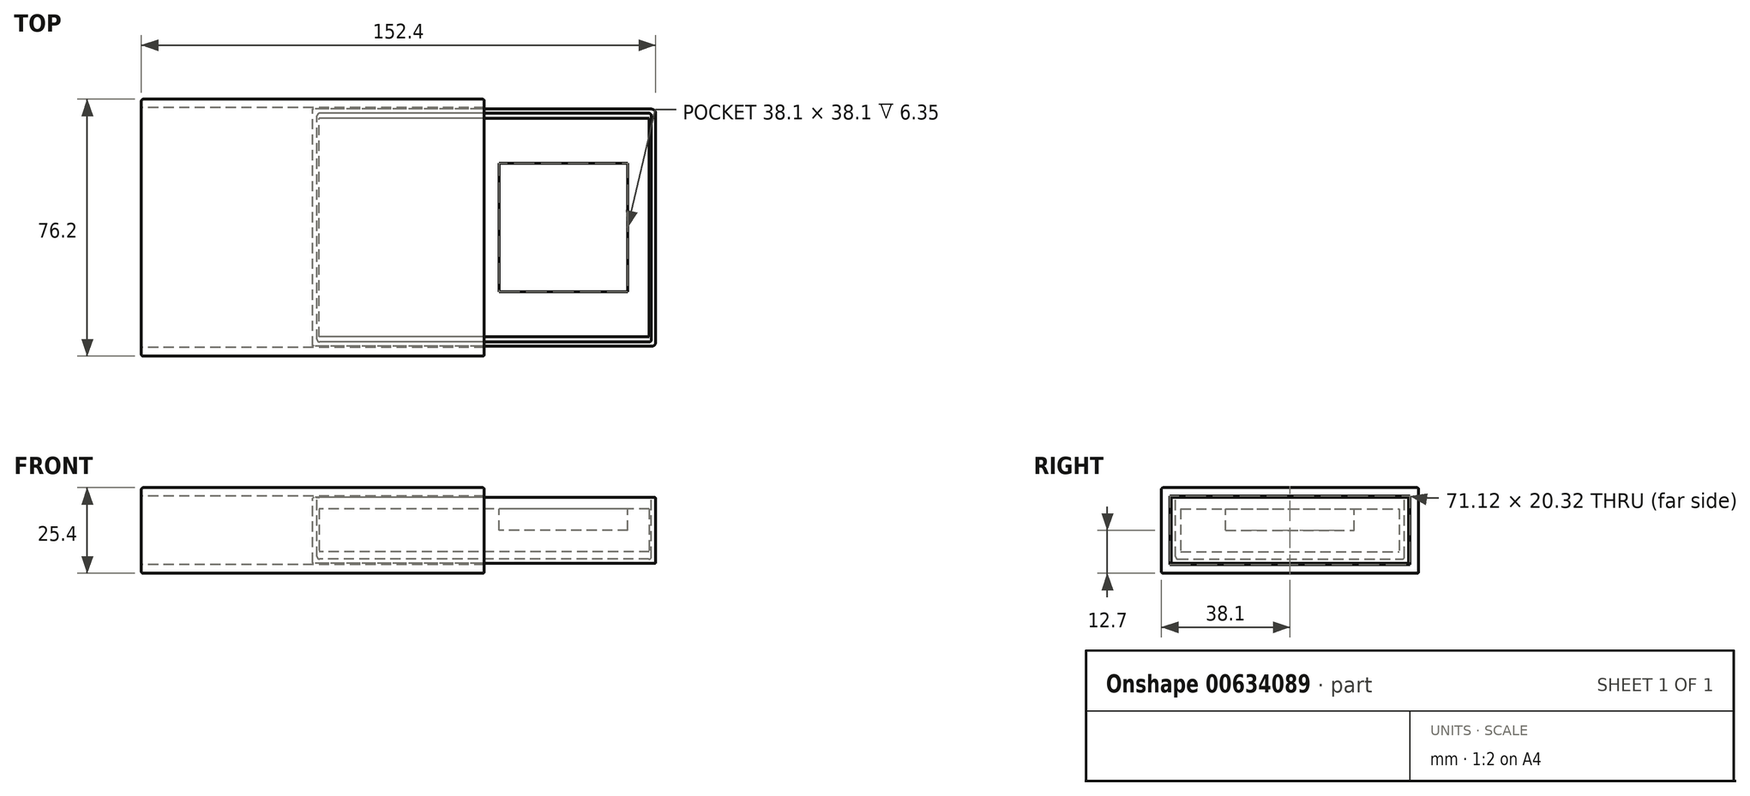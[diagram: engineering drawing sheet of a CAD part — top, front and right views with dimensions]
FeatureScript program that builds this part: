
annotation { "Feature Type Name" : "Feature", "Feature Type Description" : "" }
export const myFeature = defineFeature(function(context is Context, id is Id, definition is map)
    precondition{}
    {
        {
            var Q0;
            Q0=qCreatedBy(makeId("Front.planeOp"),FACE);
            var sketch = newSketch(context, id + "F0", { "sketchPlane" : qUnion([Q0])});
            skLineSegment(sketch, "E0.bottom", {"start": v(50.8, -12.7) * mm, "end": v(-50.8, -12.7) * mm});
            skLineSegment(sketch, "E0.top", {"start": v(50.8, 12.7) * mm, "end": v(-50.8, 12.7) * mm});
            skLineSegment(sketch, "E0.left", {"start": v(50.8, -12.7) * mm, "end": v(50.8, 12.7) * mm});
            skLineSegment(sketch, "E0.right", {"start": v(-50.8, -12.7) * mm, "end": v(-50.8, 12.7) * mm});
            skPoint(sketch, "E0.middle", {"position": v(0, 0) * mm});
            skSolve(sketch);
        }
        {
            var Q0;
            Q0 = qSketchRegion(id + "F0", true);
            extrude(context, id + "F1", {"entities" : qUnion([Q0]), "endBound" : BoundingType.SYMMETRIC, "depth" : 76.2 * mm, "offsetDistance" : 25.4 * mm});
        }
        {
            var Q0;
            Q0=makeQuery(id+"F1.opExtrude","SWEPT_FACE",FACE,{"disambiguationData":[OSD([sQuery(id+"F0.wireOp",EDGE,"E0.left")])]});
            var Q1;
            Q1=makeQuery(id+"F1.opExtrude","SWEPT_FACE",FACE,{"disambiguationData":[OSD([sQuery(id+"F0.wireOp",EDGE,"E0.right")])]});
            shell(context, id + "F2", {"entities" : qUnion([Q0, Q1]), "thickness" : 2.54 * mm});
        }
        {
            var Q0;
            Q0=makeQuery(id+"F1.opExtrude","SWEPT_FACE",FACE,{"disambiguationData":[OSD([sQuery(id+"F0.wireOp",EDGE,"E0.top")])]});
            var Q1;
            Q1=makeQuery(id+"F1.opExtrude","SWEPT_FACE",FACE,{"disambiguationData":[OSD([sQuery(id+"F0.wireOp",EDGE,"E0.bottom")])]});
            var Q2;
            Q2=makeQuery(id+"F1.opExtrude","CAP_EDGE",EDGE,{"disambiguationData":[OSD([sQuery(id+"F0.wireOp",EDGE,"E0.left")])],"isStart":false});
            var Q3;
            Q3=makeQuery(id+"F1.opExtrude","CAP_EDGE",EDGE,{"disambiguationData":[OSD([sQuery(id+"F0.wireOp",EDGE,"E0.left")])],"isStart":true});
            var Q4;
            Q4=makeQuery(id+"F1.opExtrude","CAP_EDGE",EDGE,{"disambiguationData":[OSD([sQuery(id+"F0.wireOp",EDGE,"E0.right")])],"isStart":true});
            var Q5;
            Q5=makeQuery(id+"F1.opExtrude","CAP_EDGE",EDGE,{"disambiguationData":[OSD([sQuery(id+"F0.wireOp",EDGE,"E0.right")])],"isStart":false});
            fillet(context, id + "F3", {"entities" : qUnion([Q0, Q1, Q2, Q3, Q4, Q5]), "radius" : 0.5 * mm, "tangentPropagation" : true, "allowEdgeOverflow" : false});
        }
        {
            var Q0;
            Q0=qCreatedBy(makeId("Right.planeOp"),FACE);
            var sketch = newSketch(context, id + "F4", { "sketchPlane" : qUnion([Q0])});
            skLineSegment(sketch, "E1.0", {"start": v(-35.56, 10.16) * mm, "end": v(35.56, 10.16) * mm, "construction": true});
            skLineSegment(sketch, "E2.0", {"start": v(-35.56, -10.16) * mm, "end": v(-35.56, 10.16) * mm, "construction": true});
            skLineSegment(sketch, "E3.0", {"start": v(-35.56, -10.16) * mm, "end": v(35.56, -10.16) * mm, "construction": true});
            skLineSegment(sketch, "E4.0", {"start": v(35.56, -10.16) * mm, "end": v(35.56, 10.16) * mm, "construction": true});
            skLineSegment(sketch, "E5.0", {"start": v(-35.18, 9.78) * mm, "end": v(35.18, 9.78) * mm});
            skLineSegment(sketch, "E5.1", {"start": v(-35.18, -9.78) * mm, "end": v(-35.18, 9.78) * mm});
            skLineSegment(sketch, "E5.2", {"start": v(-35.18, -9.78) * mm, "end": v(35.18, -9.78) * mm});
            skLineSegment(sketch, "E5.3", {"start": v(35.18, -9.78) * mm, "end": v(35.18, 9.78) * mm});
            skSolve(sketch);
        }
        {
            var Q0;
            Q0 = qSketchRegion(id + "F4", true);
            extrude(context, id + "F5", {"entities" : qUnion([Q0]), "endBound" : BoundingType.SYMMETRIC, "depth" : 101.6 * mm, "offsetDistance" : 25.4 * mm});
        }
        {
            var Q0;
            Q0=makeQuery(id+"F5.opExtrude","SWEPT_FACE",FACE,{"disambiguationData":[OSD([sQuery(id+"F4.wireOp",EDGE,"E5.0")])]});
            shell(context, id + "F6", {"entities" : qUnion([Q0]), "thickness" : 1.27 * mm});
        }
        {
            var Q0;
            Q0=makeQuery(id+"F6.opShell","OFFSET_FACE",FACE,{"disambiguationData":[OSD([sQuery(id+"F4.wireOp",EDGE,"E5.2")])]});
            var Q1;
            {var subQ0=sQuery(id+"F4.wireOp",EDGE,"E5.3");Q1=makeQuery(id+"F6.opShell","OFFSET_EDGE",EDGE,{"disambiguationData":[OSD([subQ0]),TDD([makeQuery(id+"F5.opExtrude","CAP_EDGE",EDGE,{"disambiguationData":[OSD([subQ0])],"isStart":true})])]});}
            var Q2;
            {var subQ0=sQuery(id+"F4.wireOp",EDGE,"E5.1");Q2=makeQuery(id+"F6.opShell","OFFSET_EDGE",EDGE,{"disambiguationData":[OSD([subQ0]),TDD([makeQuery(id+"F5.opExtrude","CAP_EDGE",EDGE,{"disambiguationData":[OSD([subQ0])],"isStart":true})])]});}
            var Q3;
            {var subQ0=sQuery(id+"F4.wireOp",EDGE,"E5.1");Q3=makeQuery(id+"F6.opShell","OFFSET_EDGE",EDGE,{"disambiguationData":[OSD([subQ0]),TDD([makeQuery(id+"F5.opExtrude","CAP_EDGE",EDGE,{"disambiguationData":[OSD([subQ0])],"isStart":false})])]});}
            var Q4;
            {var subQ0=sQuery(id+"F4.wireOp",EDGE,"E5.3");Q4=makeQuery(id+"F6.opShell","OFFSET_EDGE",EDGE,{"disambiguationData":[OSD([subQ0]),TDD([makeQuery(id+"F5.opExtrude","CAP_EDGE",EDGE,{"disambiguationData":[OSD([subQ0])],"isStart":false})])]});}
            fillet(context, id + "F7", {"entities" : qUnion([Q0, Q1, Q2, Q3, Q4]), "radius" : 0.76 * mm, "tangentPropagation" : true, "allowEdgeOverflow" : false});
        }
        {
            var Q0;
            Q0=qCreatedBy(makeId("Top.planeOp"),FACE);
            var sketch = newSketch(context, id + "F8", { "sketchPlane" : qUnion([Q0])});
            skLineSegment(sketch, "E6.bottom", {"start": v(48.9, -32.39) * mm, "end": v(-48.9, -32.39) * mm});
            skLineSegment(sketch, "E6.top", {"start": v(48.9, 32.39) * mm, "end": v(-48.9, 32.38) * mm});
            skLineSegment(sketch, "E6.left", {"start": v(48.9, -32.39) * mm, "end": v(48.9, 32.38) * mm});
            skLineSegment(sketch, "E6.right", {"start": v(-48.9, -32.39) * mm, "end": v(-48.9, 32.38) * mm});
            skPoint(sketch, "E6.middle", {"position": v(0, 0) * mm});
            skSolve(sketch);
        }
        {
            var Q0;
            Q0 = qSketchRegion(id + "F8", true);
            extrude(context, id + "F9", {"entities" : qUnion([Q0]), "depth" : 6.35 * mm, "offsetDistance" : 25.4 * mm, "hasSecondDirection" : true, "secondDirectionOppositeDirection" : true, "secondDirectionDepth" : 6.35 * mm});
        }
        {
            var Q0;
            Q0=makeQuery(id+"F9.opExtrude","CAP_FACE",FACE,{"disambiguationData":[OSD([sQuery(id+"F8.wireOp",EDGE,"E6.bottom"),sQuery(id+"F8.wireOp",EDGE,"E6.top"),sQuery(id+"F8.wireOp",EDGE,"E6.left"),sQuery(id+"F8.wireOp",EDGE,"E6.right")])],"isStart":false});
            var sketch = newSketch(context, id + "F10", { "sketchPlane" : qUnion([Q0])});
            skLineSegment(sketch, "E7.bottom", {"start": v(42.55, -19.05) * mm, "end": v(4.45, -19.05) * mm});
            skLineSegment(sketch, "E7.top", {"start": v(42.55, 19.05) * mm, "end": v(4.45, 19.05) * mm});
            skLineSegment(sketch, "E7.left", {"start": v(42.55, -19.05) * mm, "end": v(42.55, 19.05) * mm});
            skLineSegment(sketch, "E7.right", {"start": v(4.45, -19.05) * mm, "end": v(4.45, 19.05) * mm});
            skPoint(sketch, "E7.middle", {"position": v(23.5, 0) * mm});
            skPoint(sketch, "E7.middle.positionSnap0", {"position": v(48.9, 0) * mm});
            skPoint(sketch, "E7.centerSnap0", {"position": v(48.9, 0) * mm});
            skSolve(sketch);
        }
        {
            var Q0;
            Q0 = qSketchRegion(id + "F10", true);
            extrude(context, id + "F11", {"entities" : qUnion([Q0]), "operationType" : NewBodyOperationType.REMOVE, "oppositeDirection" : true, "depth" : 6.35 * mm, "offsetDistance" : 25.4 * mm});
        }
        {
            var Q0;
            Q0=makeQuery(id+"F5.opExtrude","CAP_EDGE",EDGE,{"disambiguationData":[OSD([sQuery(id+"F4.wireOp",EDGE,"E5.1")])],"isStart":false});
            var Q1;
            Q1=makeQuery(id+"F5.opExtrude","CAP_EDGE",EDGE,{"disambiguationData":[OSD([sQuery(id+"F4.wireOp",EDGE,"E5.3")])],"isStart":false});
            fillet(context, id + "F12", {"entities" : qUnion([Q0, Q1]), "radius" : 1.27 * mm, "tangentPropagation" : true, "allowEdgeOverflow" : false});
        }
        {
            var Q0;
            Q0=makeQuery(id+"F5.opExtrude","SWEPT_FACE",FACE,{"disambiguationData":[OSD([sQuery(id+"F4.wireOp",EDGE,"E5.0")])]});
            var Q1;
            Q1=makeQuery(id+"F5.opExtrude","SWEPT_FACE",FACE,{"disambiguationData":[OSD([sQuery(id+"F4.wireOp",EDGE,"E5.2")])]});
            fillet(context, id + "F13", {"entities" : qUnion([Q0, Q1]), "radius" : 0.25 * mm, "tangentPropagation" : true, "allowEdgeOverflow" : false});
        }
        {
            var Q0;
            Q0=makeQuery(id+"F5.opExtrude","SWEPT_BODY",BODY,{"disambiguationData":[OSD([sQuery(id+"F4.wireOp",EDGE,"E5.0"),sQuery(id+"F4.wireOp",EDGE,"E5.1"),sQuery(id+"F4.wireOp",EDGE,"E5.2"),sQuery(id+"F4.wireOp",EDGE,"E5.3")])]});
            var Q1;
            Q1=makeQuery(id+"F9.opExtrude","SWEPT_BODY",BODY,{"disambiguationData":[OSD([sQuery(id+"F8.wireOp",EDGE,"E6.bottom"),sQuery(id+"F8.wireOp",EDGE,"E6.top"),sQuery(id+"F8.wireOp",EDGE,"E6.left"),sQuery(id+"F8.wireOp",EDGE,"E6.right")])]});
            var Q2;
            Q2=qCreatedBy(makeId("Right.planeOp"),FACE);
            transform(context, id + "F14", {"entities" : qUnion([Q0, Q1]), "transformType" : TransformType.TRANSLATION_DISTANCE, "transformDirection" : qUnion([Q2]), "distance" : 50.8 * mm, "makeCopy" : false});
        }
    });
